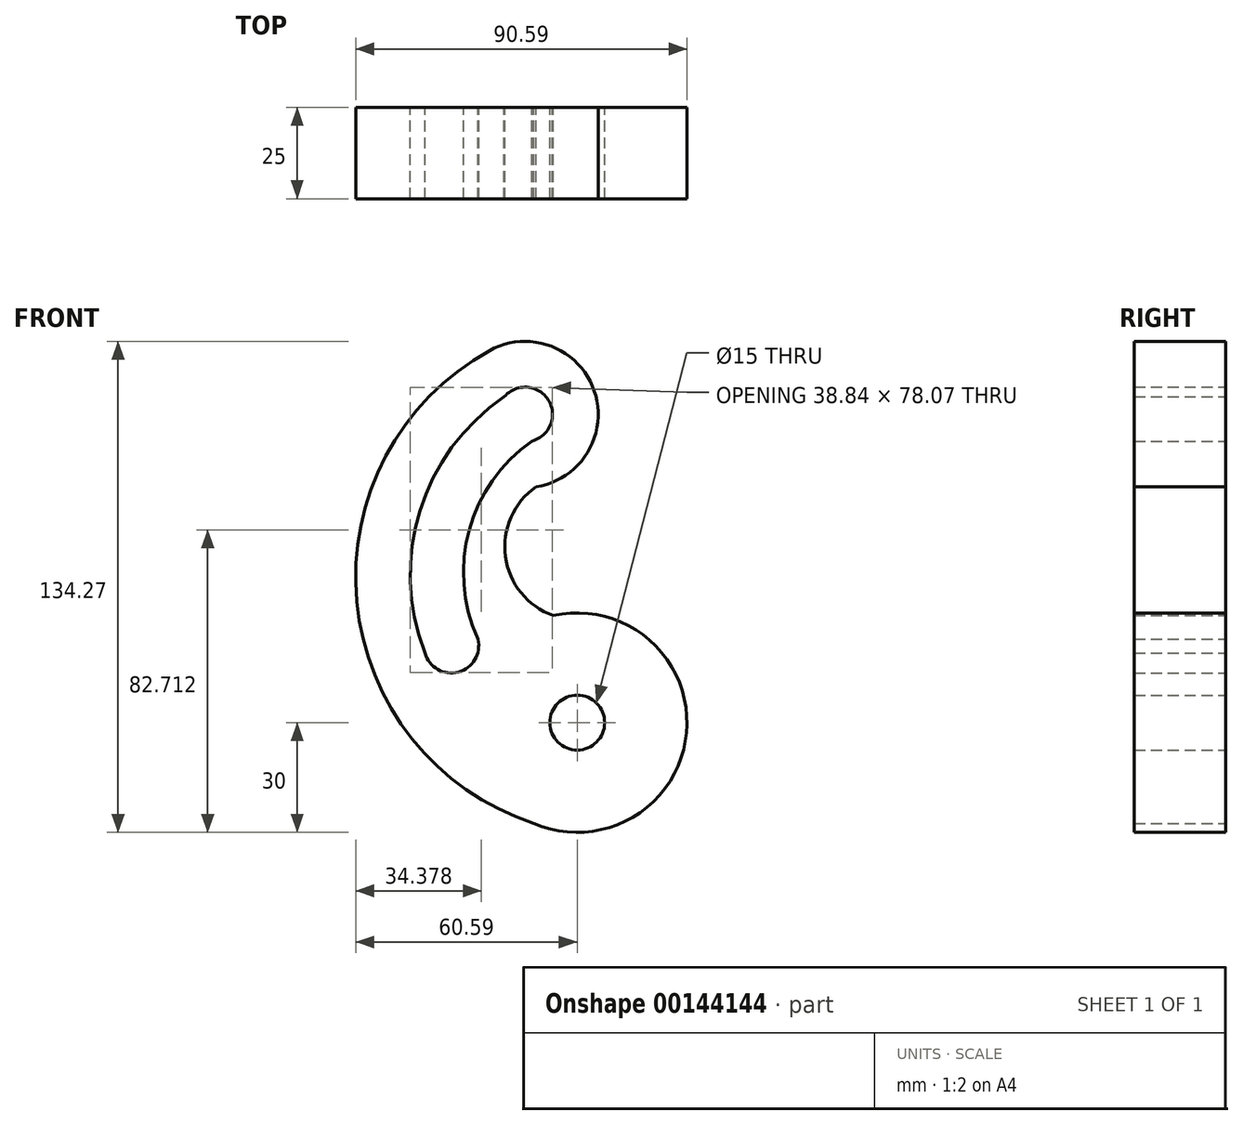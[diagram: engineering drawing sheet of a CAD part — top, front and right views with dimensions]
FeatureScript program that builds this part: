
annotation { "Feature Type Name" : "Feature", "Feature Type Description" : "" }
export const myFeature = defineFeature(function(context is Context, id is Id, definition is map)
    precondition{}
    {
        {
            var Q0;
            Q0=qCreatedBy(makeId("Front.planeOp"),FACE);
            var sketch = newSketch(context, id + "F0", { "sketchPlane" : qUnion([Q0])});
            skLineSegment(sketch, "E0", {"start": v(0, 0) * mm, "end": v(-82.38, -21.65) * mm, "construction": true});
            skLineSegment(sketch, "E1", {"start": v(0, 0) * mm, "end": v(-30.64, 116.61) * mm, "construction": true});
            skArc(sketch, "E2", {"start": v(-11.9, -57.54) * mm, "mid": v(29.87, -32.8) * mm, "end": v(-6.57, -0.73) * mm});
            skCircle(sketch, "E3", {"center": v(0, -30) * mm, "radius": 7.5 * mm});
            skArc(sketch, "E4", {"start": v(-11.25, 34.5) * mm, "mid": v(4.67, 60.73) * mm, "end": v(-23.96, 71.76) * mm});
            skArc(sketch, "E5", {"start": v(-12.35, 47.01) * mm, "mid": v(-7.91, 58.26) * mm, "end": v(-19.97, 59.13) * mm});
            skArc(sketch, "E6", {"start": v(-11.25, 34.5) * mm, "mid": v(-19.5, 14.56) * mm, "end": v(-4.83, -1.27) * mm});
            skArc(sketch, "E7", {"start": v(-23.96, 71.76) * mm, "mid": v(-60.28, 3.15) * mm, "end": v(-11.9, -57.54) * mm});
            skArc(sketch, "E8", {"start": v(-12.35, 47.01) * mm, "mid": v(-29.57, 22.62) * mm, "end": v(-27.15, -7.13) * mm});
            skArc(sketch, "E9", {"start": v(-16.17, 61.52) * mm, "mid": v(-42.33, 30) * mm, "end": v(-41.65, -10.94) * mm});
            skArc(sketch, "E10", {"start": v(-41.65, -10.94) * mm, "mid": v(-32.53, -16.14) * mm, "end": v(-27.15, -7.13) * mm});
            skArc(sketch, "E11", {"start": v(-14.26, 54.27) * mm, "mid": v(-34.95, 26.08) * mm, "end": v(-34.44, -8.89) * mm, "construction": true});
            skSolve(sketch);
        }
        {
            var Q0;
            Q0 = qSketchRegion(id + "F0", true);
            extrude(context, id + "F1", {"entities" : qUnion([Q0]), "depth" : 25 * mm});
        }
    });
